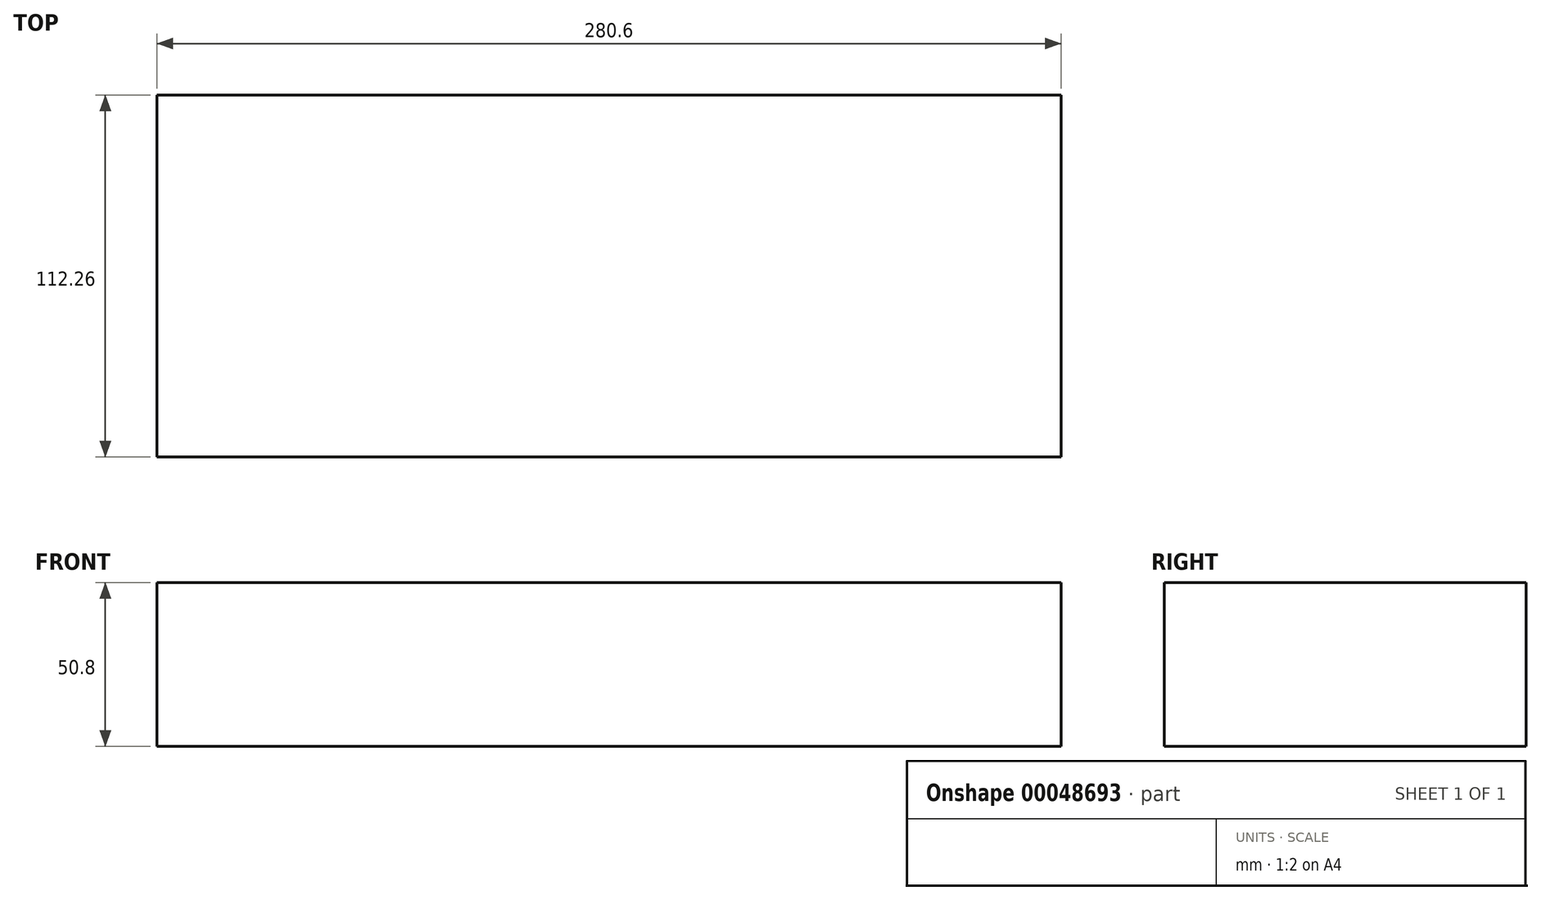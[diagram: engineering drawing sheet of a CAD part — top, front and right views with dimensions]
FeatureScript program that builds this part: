
annotation { "Feature Type Name" : "Feature", "Feature Type Description" : "" }
export const myFeature = defineFeature(function(context is Context, id is Id, definition is map)
    precondition{}
    {
        {
            var Q0;
            Q0=qCreatedBy(makeId("Top.planeOp"),FACE);
            var sketch = newSketch(context, id + "F0", { "sketchPlane" : qUnion([Q0])});
            skLineSegment(sketch, "E0.rect.bottom", {"start": v(-140.3, -56.13) * mm, "end": v(140.3, -56.13) * mm});
            skLineSegment(sketch, "E0.rect.top", {"start": v(-140.3, 56.13) * mm, "end": v(140.3, 56.13) * mm});
            skLineSegment(sketch, "E0.rect.left", {"start": v(-140.3, -56.13) * mm, "end": v(-140.3, 56.13) * mm});
            skLineSegment(sketch, "E0.rect.right", {"start": v(140.3, -56.13) * mm, "end": v(140.3, 56.13) * mm});
            skPoint(sketch, "E0.rect.middle", {"position": v(0, 0) * mm});
            skLineSegment(sketch, "E1", {"start": v(-105.17, 56.13) * mm, "end": v(-105.17, -56.13) * mm});
            skLineSegment(sketch, "E2", {"start": v(-140.3, 18.62) * mm, "end": v(-105.17, 18.62) * mm});
            skSolve(sketch);
        }
        {
            var Q0;
            Q0 = qSketchRegion(id + "F0", true);
            extrude(context, id + "F1", {"entities" : qUnion([Q0]), "depth" : 50.8 * mm});
        }
    });
